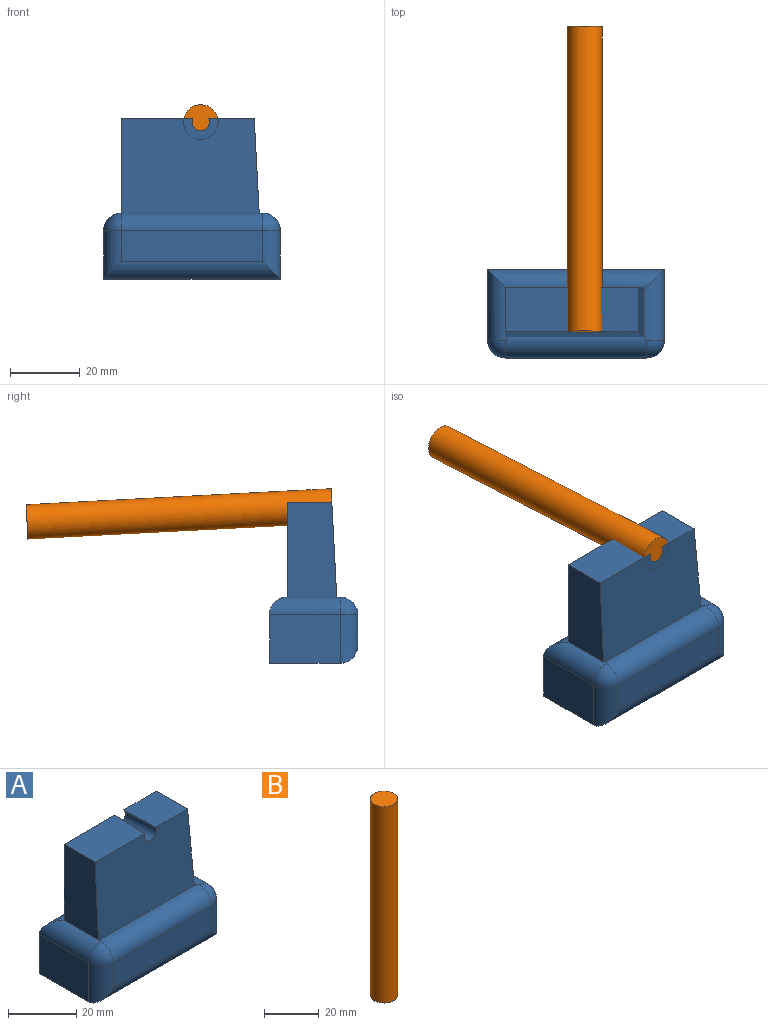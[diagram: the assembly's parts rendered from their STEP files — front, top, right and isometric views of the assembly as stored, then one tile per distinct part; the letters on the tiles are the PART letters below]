
ASSEMBLY  parts=2 mates=2
PART A: 21 faces, bbox 50.8x25.4x46.9 mm
  f0: plane 13.55x12.82mm, normal (0,0,1), area 170.5mm2, adj f16,f18,f19,f20
  f1: plane 21x12.82mm, normal (0,0,1), area 265.9mm2, adj f16,f17,f18,f20
  f2: plane 20.32x13.97mm, normal (1,0,0), area 283.9mm2, adj f3,f5,f7,f10
  f3: plane 50.8x13.97mm, normal (0,1,0), area 709.7mm2, adj f2,f5,f6,f8
  f4: plane 40.64x8.89mm, normal (0,-1,0), area 361.3mm2, adj f10,f12,f13,f15
  f5: plane 50.8x20.32mm, normal (0,0,-1), area 1032.3mm2, adj f2,f3,f6,f13
  f6: plane 20.32x13.97mm, normal (-1,0,0), area 283.9mm2, adj f3,f5,f11,f15
  f7: cylinder r=5.08mm len=20.32mm, axis (0,1,0), area 161.7mm2, adj f2,f8,f9,f12,f19
  f8: cylinder r=5.08mm len=50.8mm, axis (-1,0,0), area 376.4mm2, adj f3,f7,f11,f16,f19
  f9: sphere r=5.08mm, area 40.5mm2, adj f7,f10,f12
  f10: cylinder r=5.08mm len=13.97mm, axis (0,0,1), area 96.7mm2, adj f2,f4,f9,f13
  f11: cylinder r=5.08mm len=20.32mm, axis (0,-1,0), area 147.9mm2, adj f6,f8,f12,f14,f17,f18
  f12: cylinder r=5.08mm len=40.64mm, axis (1,0,0), area 363.9mm2, adj f4,f7,f9,f11,f14,f18
  f13: cylinder r=5.08mm len=50.8mm, axis (-1,0,0), area 375.9mm2, adj f4,f5,f10,f15
  f14: sphere r=5.08mm, area 40.5mm2, adj f11,f12,f15
  f15: cylinder r=5.08mm len=13.97mm, axis (0,0,-1), area 96.7mm2, adj f4,f6,f13,f14
  f16: plane 39.64x27.18mm, normal (0,1,0), area 1040.4mm2, adj f0,f1,f8,f17,f19,f20
  f17: plane 27.18x14.24mm, normal (-1,0,0), area 367.7mm2, adj f1,f11,f16,f18
  f18: plane 39.65x27.28mm, normal (0,-1,0.05), area 1048.5mm2, adj f0,f1,f11,f12,f17,f19,f20
  f19: plane 27.28x14.25mm, normal (1,0,0.05), area 369.5mm2, adj f0,f7,f8,f16,f18
  f20: cylinder r=2.5mm len=13.22mm, axis (0,-1,0.05), area 139mm2, adj f0,f1,f16,f18
PART B: 3 faces, bbox 10x10x87.8 mm
  f0: cylinder r=5mm len=87.8mm, axis (0,0,-1), area 2758.3mm2, adj f1,f2
  f1: plane 10x10mm, normal (0,0,1), area 78.5mm2, adj f0
  f2: plane 10x10mm, normal (0,0,-1), area 78.5mm2, adj f0
PLACE A t=(-11.51,4.6,-6.95)mm fixed
PLACE B rot(axis=(0.57,-0.57,0.6),118.3deg) t=(16.4,112.42,49.53)mm
MATE planar B.f0 <-> A.f18  axis (0,-1,0.05) through (16.4,24.74,54.13)mm
MATE cylindrical A.f20 <-> B.f0  axis (0,-1,0.05) through (16.4,31.28,53.78)mm
